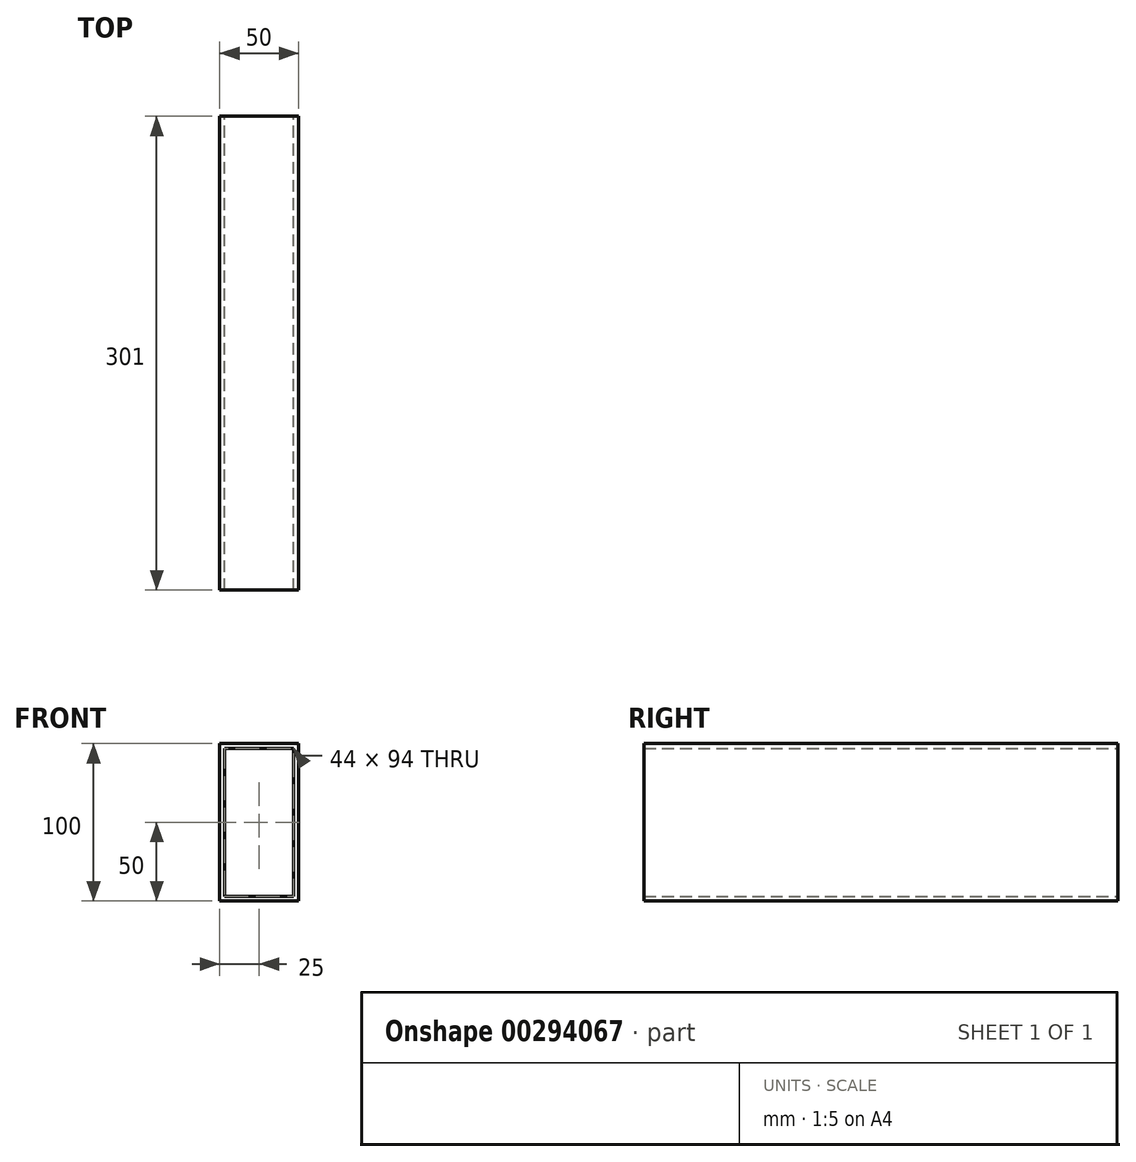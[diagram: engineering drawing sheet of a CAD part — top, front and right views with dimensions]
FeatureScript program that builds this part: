
annotation { "Feature Type Name" : "Feature", "Feature Type Description" : "" }
export const myFeature = defineFeature(function(context is Context, id is Id, definition is map)
    precondition{}
    {
        {
            var Q0;
            Q0=qCreatedBy(makeId("Front.planeOp"),FACE);
            var sketch = newSketch(context, id + "F0", { "sketchPlane" : qUnion([Q0])});
            skLineSegment(sketch, "E0", {"start": v(0, 0) * mm, "end": v(0, 100) * mm});
            skLineSegment(sketch, "E1", {"start": v(0, 100) * mm, "end": v(50, 100) * mm});
            skLineSegment(sketch, "E2", {"start": v(50, 100) * mm, "end": v(50, 0) * mm});
            skLineSegment(sketch, "E3", {"start": v(50, 0) * mm, "end": v(0, 0) * mm});
            skLineSegment(sketch, "E4", {"start": v(3, 97) * mm, "end": v(3, 3) * mm});
            skLineSegment(sketch, "E5", {"start": v(3, 3) * mm, "end": v(47, 3) * mm});
            skLineSegment(sketch, "E6", {"start": v(47, 3) * mm, "end": v(47, 97) * mm});
            skLineSegment(sketch, "E7", {"start": v(3, 97) * mm, "end": v(47, 97) * mm});
            skSolve(sketch);
        }
        {
            var Q0;
            Q0=makeQuery(id+"F0.imprint","IMPRINT",FACE,{"disambiguationData":[TD([[makeQuery(id+"F0.imprint","IMPRINT",EDGE,{"derivedFrom":sQuery(id+"F0.wireOp",EDGE,"E0")}),-1.0]])]});
            extrude(context, id + "F1", {"entities" : qUnion([Q0]), "depth" : 301 * mm});
        }
    });
